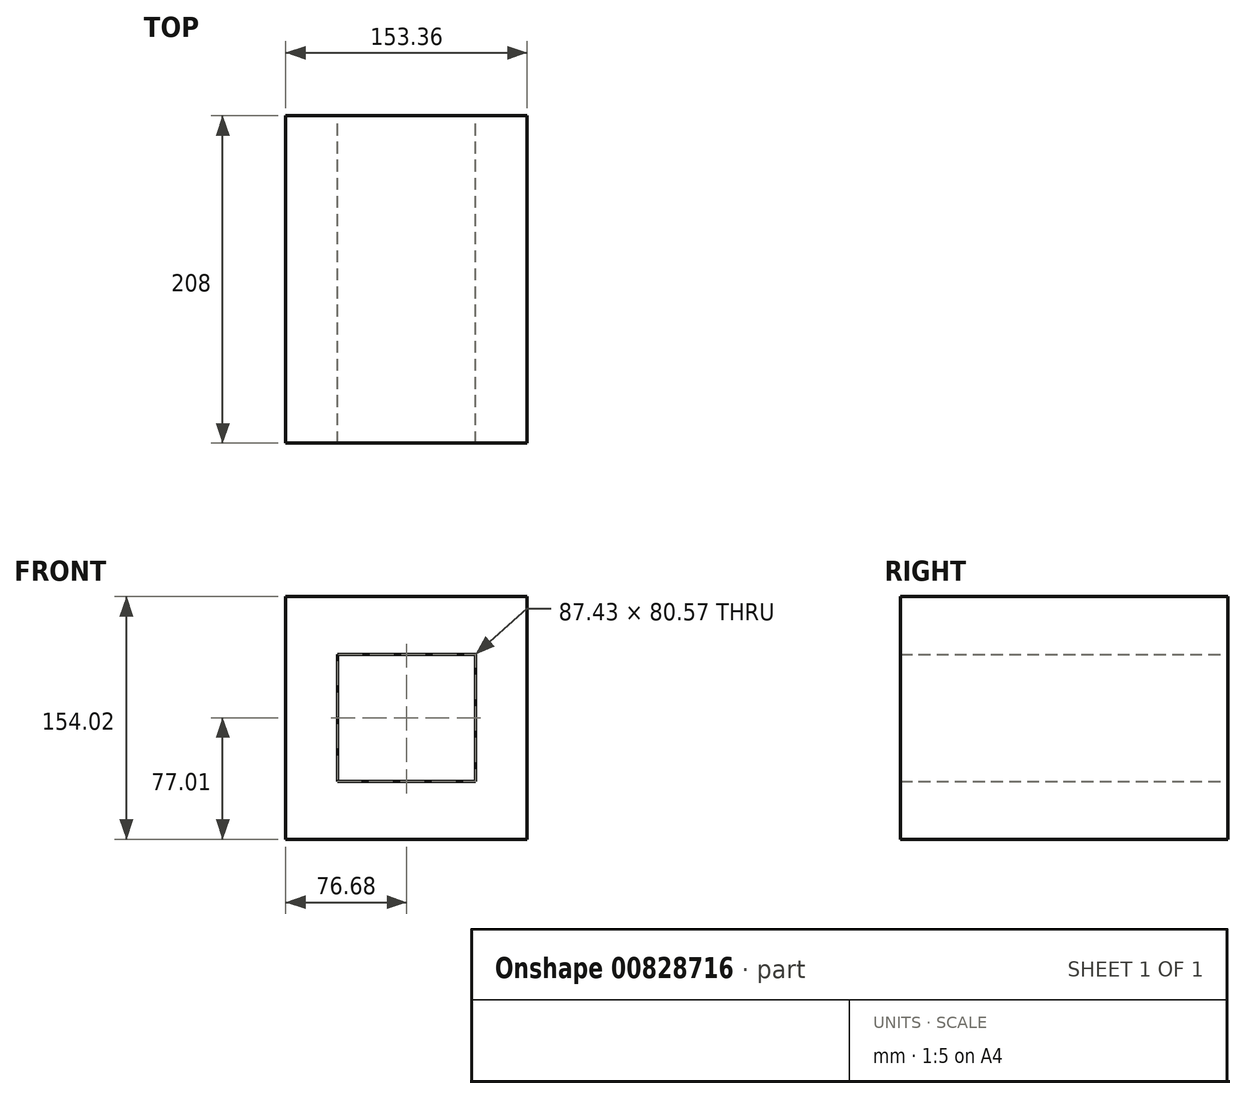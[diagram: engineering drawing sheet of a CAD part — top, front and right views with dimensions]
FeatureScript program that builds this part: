
annotation { "Feature Type Name" : "Feature", "Feature Type Description" : "" }
export const myFeature = defineFeature(function(context is Context, id is Id, definition is map)
    precondition{}
    {
        {
            var Q0;
            Q0=qCreatedBy(makeId("Front.planeOp"),FACE);
            var sketch = newSketch(context, id + "F0", { "sketchPlane" : qUnion([Q0])});
            skLineSegment(sketch, "E0.bottom", {"start": v(76.68, 77) * mm, "end": v(-76.68, 77) * mm});
            skLineSegment(sketch, "E0.top", {"start": v(76.68, -77) * mm, "end": v(-76.68, -77) * mm});
            skLineSegment(sketch, "E0.left", {"start": v(76.68, 77) * mm, "end": v(76.68, -77) * mm});
            skLineSegment(sketch, "E0.right", {"start": v(-76.68, 77) * mm, "end": v(-76.68, -77) * mm});
            skPoint(sketch, "E0.middle", {"position": v(0, 0) * mm});
            skLineSegment(sketch, "E1.bottom", {"start": v(43.72, 40.29) * mm, "end": v(-43.72, 40.29) * mm});
            skLineSegment(sketch, "E1.top", {"start": v(43.72, -40.29) * mm, "end": v(-43.72, -40.29) * mm});
            skLineSegment(sketch, "E1.left", {"start": v(43.72, 40.29) * mm, "end": v(43.72, -40.29) * mm});
            skLineSegment(sketch, "E1.right", {"start": v(-43.72, 40.29) * mm, "end": v(-43.72, -40.29) * mm});
            skSolve(sketch);
        }
        {
            var Q0;
            Q0=makeQuery(id+"F0.imprint","IMPRINT",FACE,{"disambiguationData":[TD([[makeQuery(id+"F0.imprint","IMPRINT",EDGE,{"derivedFrom":sQuery(id+"F0.wireOp",EDGE,"E0.bottom")}),1.0]])]});
            extrude(context, id + "F1", {"entities" : qUnion([Q0]), "depth" : 35 * mm, "offsetDistance" : 25.4 * mm});
        }
        {
            var Q0;
            Q0 = qSketchRegion(id + "F0", true);
            extrude(context, id + "F2", {"entities" : qUnion([Q0]), "operationType" : NewBodyOperationType.ADD, "depth" : 208 * mm, "offsetDistance" : 25 * mm});
        }
    });
